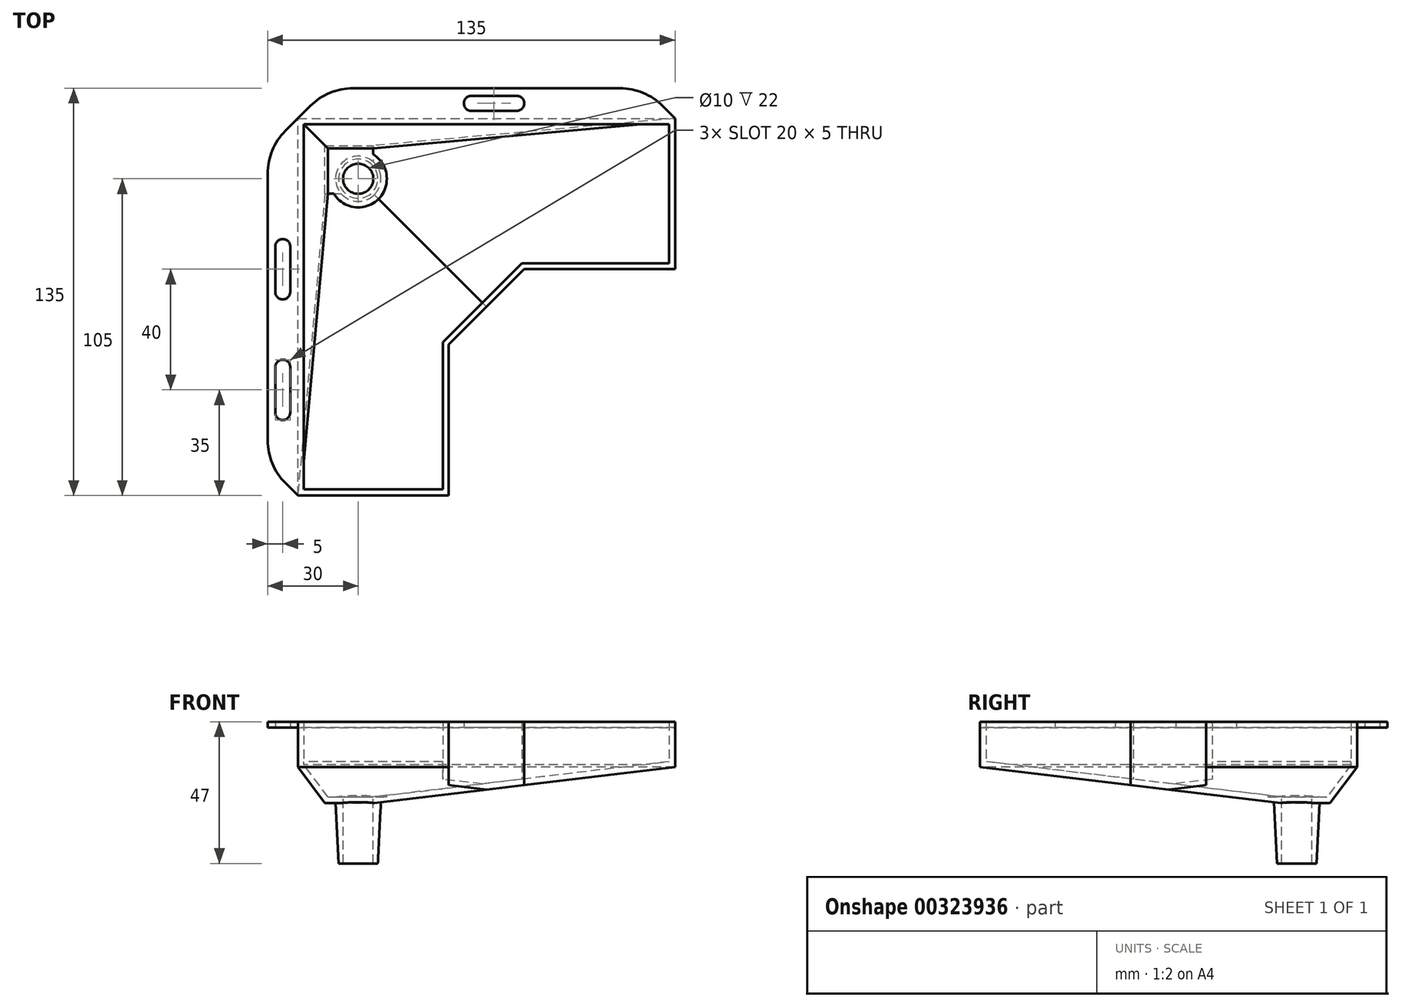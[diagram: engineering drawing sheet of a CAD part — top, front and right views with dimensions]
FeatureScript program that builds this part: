
annotation { "Feature Type Name" : "Feature", "Feature Type Description" : "" }
export const myFeature = defineFeature(function(context is Context, id is Id, definition is map)
    precondition{}
    {
        {
            var Q0;
            Q0=qCreatedBy(makeId("Top.planeOp"),FACE);
            var sketch = newSketch(context, id + "F0", { "sketchPlane" : qUnion([Q0])});
            skLineSegment(sketch, "E0", {"start": v(-70, -85) * mm, "end": v(-70, 40) * mm});
            skLineSegment(sketch, "E1", {"start": v(-70, 40) * mm, "end": v(55, 40) * mm});
            skLineSegment(sketch, "E2", {"start": v(55, 40) * mm, "end": v(55, -10) * mm});
            skLineSegment(sketch, "E3", {"start": v(55, -10) * mm, "end": v(5, -10) * mm});
            skLineSegment(sketch, "E4", {"start": v(5, -10) * mm, "end": v(-20, -35) * mm});
            skLineSegment(sketch, "E5", {"start": v(-20, -35) * mm, "end": v(-20, -85) * mm});
            skLineSegment(sketch, "E6", {"start": v(-20, -85) * mm, "end": v(-70, -85) * mm});
            skLineSegment(sketch, "E7", {"start": v(55, 40) * mm, "end": v(55, 50) * mm});
            skLineSegment(sketch, "E8", {"start": v(55, 50) * mm, "end": v(-80, 50) * mm});
            skLineSegment(sketch, "E9", {"start": v(-80, 50) * mm, "end": v(-80, -85) * mm});
            skLineSegment(sketch, "E10", {"start": v(-80, -85) * mm, "end": v(-70, -85) * mm});
            skCircle(sketch, "E11", {"center": v(-50, 20) * mm, "radius": 7.5 * mm});
            skCircle(sketch, "E12", {"center": v(-50, 20) * mm, "radius": 6 * mm});
            skCircle(sketch, "E13", {"center": v(-50, 20) * mm, "radius": 5 * mm});
            skSolve(sketch);
        }
        {
            var Q0;
            Q0=makeQuery(id+"F0.imprint","IMPRINT",FACE,{"disambiguationData":[TD([[makeQuery(id+"F0.imprint","IMPRINT",EDGE,{"derivedFrom":sQuery(id+"F0.wireOp",EDGE,"E0")}),1.0]])]});
            extrude(context, id + "F1", {"entities" : qUnion([Q0]), "depth" : 2 * mm});
        }
        {
            var Q0;
            Q0=makeQuery(id+"F0.imprint","IMPRINT",FACE,{"disambiguationData":[TD([[makeQuery(id+"F0.imprint","IMPRINT",EDGE,{"derivedFrom":sQuery(id+"F0.wireOp",EDGE,"E0")}),-1.0]])]});
            extrude(context, id + "F2", {"entities" : qUnion([Q0]), "operationType" : NewBodyOperationType.ADD, "depth" : 2 * mm, "hasSecondDirection" : true, "secondDirectionOppositeDirection" : true, "secondDirectionDepth" : 25 * mm});
        }
        {
            var Q0;
            Q0=makeQuery(id+"F0.imprint","IMPRINT",FACE,{"disambiguationData":[TD([[makeQuery(id+"F0.imprint","IMPRINT",EDGE,{"derivedFrom":sQuery(id+"F0.wireOp",EDGE,"E11")}),1.0]])]});
            var Q1;
            Q1=makeQuery(id+"F0.imprint","IMPRINT",FACE,{"disambiguationData":[TD([[makeQuery(id+"F0.imprint","IMPRINT",EDGE,{"derivedFrom":sQuery(id+"F0.wireOp",EDGE,"E12")}),1.0]])]});
            extrude(context, id + "F3", {"entities" : qUnion([Q0, Q1]), "operationType" : NewBodyOperationType.ADD, "oppositeDirection" : true, "depth" : 45 * mm, "hasSecondDirection" : true, "secondDirectionOppositeDirection" : true, "secondDirectionDepth" : 23 * mm});
        }
        {
            var Q0;
            Q0=makeQuery(id+"F3.opExtrude","CAP_EDGE",EDGE,{"disambiguationData":[OSD([sQuery(id+"F0.wireOp",EDGE,"E11")])],"isStart":false});
            chamfer(context, id + "F4", {"entities" : qUnion([Q0]), "chamferType" : ChamferType.TWO_OFFSETS, "width1" : 20 * mm, "oppositeDirection" : false, "width2" : 1 * mm, "tangentPropagation" : true});
        }
        {
            var Q0;
            Q0=makeQuery(id+"F2.opExtrude","CAP_EDGE",EDGE,{"disambiguationData":[OSD([sQuery(id+"F0.wireOp",EDGE,"E2")])],"isStart":true});
            var Q1;
            Q1=makeQuery(id+"F2.opExtrude","CAP_EDGE",EDGE,{"disambiguationData":[OSD([sQuery(id+"F0.wireOp",EDGE,"E6")])],"isStart":true});
            chamfer(context, id + "F5", {"entities" : qUnion([Q0, Q1]), "chamferType" : ChamferType.TWO_OFFSETS, "width1" : 100 * mm, "oppositeDirection" : false, "width2" : 12 * mm, "tangentPropagation" : true});
        }
        {
            var Q0;
            Q0=makeQuery(id+"F2.opExtrude","CAP_EDGE",EDGE,{"disambiguationData":[OSD([sQuery(id+"F0.wireOp",EDGE,"E0")])],"isStart":true});
            var Q1;
            Q1=makeQuery(id+"F2.opExtrude","CAP_EDGE",EDGE,{"disambiguationData":[OSD([sQuery(id+"F0.wireOp",EDGE,"E1")])],"isStart":true});
            chamfer(context, id + "F6", {"entities" : qUnion([Q0, Q1]), "chamferType" : ChamferType.TWO_OFFSETS, "width1" : 9 * mm, "oppositeDirection" : false, "width2" : 12 * mm, "tangentPropagation" : true});
        }
        {
            var Q0;
            {var subQ0=sQuery(id+"F0.wireOp",EDGE,"E1");var subQ1=sQuery(id+"F0.wireOp",EDGE,"E0");Q0=makeQuery(id+"F2.boolean.opBoolean","MERGE",FACE,{"derivedFrom":[makeQuery(id+"F1.opExtrude","CAP_FACE",FACE,{"disambiguationData":[OSD([subQ1,subQ0,sQuery(id+"F0.wireOp",EDGE,"E7"),sQuery(id+"F0.wireOp",EDGE,"E8"),sQuery(id+"F0.wireOp",EDGE,"E9"),sQuery(id+"F0.wireOp",EDGE,"E10")])],"isStart":false}),makeQuery(id+"F2.opExtrude","CAP_FACE",FACE,{"disambiguationData":[OSD([subQ1,subQ0,sQuery(id+"F0.wireOp",EDGE,"E2"),sQuery(id+"F0.wireOp",EDGE,"E3"),sQuery(id+"F0.wireOp",EDGE,"E4"),sQuery(id+"F0.wireOp",EDGE,"E5"),sQuery(id+"F0.wireOp",EDGE,"E6"),sQuery(id+"F0.wireOp",EDGE,"E11")])],"isStart":false})]});}
            shell(context, id + "F7", {"entities" : qUnion([Q0]), "thickness" : 2 * mm});
        }
        {
            var Q0;
            {var subQ0=sQuery(id+"F0.wireOp",EDGE,"E1");var subQ1=sQuery(id+"F0.wireOp",EDGE,"E0");Q0=makeQuery(id+"F2.boolean.opBoolean","MERGE",FACE,{"derivedFrom":[makeQuery(id+"F1.opExtrude","CAP_FACE",FACE,{"disambiguationData":[OSD([subQ1,subQ0,sQuery(id+"F0.wireOp",EDGE,"E7"),sQuery(id+"F0.wireOp",EDGE,"E8"),sQuery(id+"F0.wireOp",EDGE,"E9"),sQuery(id+"F0.wireOp",EDGE,"E10")])],"isStart":false}),makeQuery(id+"F2.opExtrude","CAP_FACE",FACE,{"disambiguationData":[OSD([subQ1,subQ0,sQuery(id+"F0.wireOp",EDGE,"E2"),sQuery(id+"F0.wireOp",EDGE,"E3"),sQuery(id+"F0.wireOp",EDGE,"E4"),sQuery(id+"F0.wireOp",EDGE,"E5"),sQuery(id+"F0.wireOp",EDGE,"E6"),sQuery(id+"F0.wireOp",EDGE,"E11")])],"isStart":false})]});}
            extrude(context, id + "F8", {"entities" : qUnion([Q0]), "operationType" : NewBodyOperationType.REMOVE, "oppositeDirection" : true, "depth" : 25 * mm});
        }
        {
            var Q0;
            Q0=qCreatedBy(makeId("Top.planeOp"),FACE);
            var sketch = newSketch(context, id + "F9", { "sketchPlane" : qUnion([Q0])});
            skLineSegment(sketch, "E14.bottom", {"start": v(5, 42.5) * mm, "end": v(-15, 42.5) * mm});
            skLineSegment(sketch, "E14.top", {"start": v(5, 47.5) * mm, "end": v(-15, 47.5) * mm});
            skLineSegment(sketch, "E14.left", {"start": v(5, 42.5) * mm, "end": v(5, 47.5) * mm});
            skLineSegment(sketch, "E14.right", {"start": v(-15, 42.5) * mm, "end": v(-15, 47.5) * mm});
            skPoint(sketch, "E14.middle", {"position": v(-5, 45) * mm});
            skLineSegment(sketch, "E15.bottom", {"start": v(-72.5, -20) * mm, "end": v(-77.5, -20) * mm});
            skLineSegment(sketch, "E15.top", {"start": v(-72.5, 0) * mm, "end": v(-77.5, 0) * mm});
            skLineSegment(sketch, "E15.left", {"start": v(-72.5, -20) * mm, "end": v(-72.5, 0) * mm});
            skLineSegment(sketch, "E15.right", {"start": v(-77.5, -20) * mm, "end": v(-77.5, 0) * mm});
            skPoint(sketch, "E15.middle", {"position": v(-75, -10) * mm});
            skLineSegment(sketch, "E16.bottom", {"start": v(-72.5, -60) * mm, "end": v(-77.5, -60) * mm});
            skLineSegment(sketch, "E16.top", {"start": v(-72.5, -40) * mm, "end": v(-77.5, -40) * mm});
            skLineSegment(sketch, "E16.left", {"start": v(-72.5, -60) * mm, "end": v(-72.5, -40) * mm});
            skLineSegment(sketch, "E16.right", {"start": v(-77.5, -60) * mm, "end": v(-77.5, -40) * mm});
            skPoint(sketch, "E16.middle", {"position": v(-75, -50) * mm});
            skSolve(sketch);
        }
        {
            var Q0;
            Q0 = qSketchRegion(id + "F9", true);
            extrude(context, id + "F10", {"entities" : qUnion([Q0]), "operationType" : NewBodyOperationType.REMOVE, "depth" : 25 * mm});
        }
        {
            var Q0;
            Q0=makeQuery(id+"F1.opExtrude","SWEPT_EDGE",EDGE,{"disambiguationData":[OSD([sQuery(id+"F0.wireOp",EDGE,"E8"),sQuery(id+"F0.wireOp",EDGE,"E9")])]});
            chamfer(context, id + "F11", {"entities" : qUnion([Q0]), "width" : 20 * mm, "tangentPropagation" : true});
        }
        {
            var Q0;
            Q0=makeQuery(id+"F1.opExtrude","SWEPT_EDGE",EDGE,{"disambiguationData":[OSD([sQuery(id+"F0.wireOp",EDGE,"E7"),sQuery(id+"F0.wireOp",EDGE,"E8")])]});
            var Q1;
            Q1=makeQuery(id+"F1.opExtrude","SWEPT_EDGE",EDGE,{"disambiguationData":[OSD([sQuery(id+"F0.wireOp",EDGE,"E9"),sQuery(id+"F0.wireOp",EDGE,"E10")])]});
            chamfer(context, id + "F12", {"entities" : qUnion([Q0, Q1]), "width" : 10 * mm, "tangentPropagation" : true});
        }
        {
            var Q0;
            {var subQ0=sQuery(id+"F0.wireOp",EDGE,"E8");Q0=makeQuery(id+"F12.opChamfer","BLEND_EDGE",EDGE,{"blendedFrom":[makeQuery(id+"F1.opExtrude","SWEPT_EDGE",EDGE,{"disambiguationData":[OSD([sQuery(id+"F0.wireOp",EDGE,"E7"),subQ0])]}),makeQuery(id+"F1.opExtrude","SWEPT_FACE",FACE,{"disambiguationData":[OSD([subQ0])]})],"blendedInto":[makeQuery(id+"F1.opExtrude","SWEPT_FACE",FACE,{"disambiguationData":[OSD([subQ0])]})]});}
            var Q1;
            {var subQ0=sQuery(id+"F0.wireOp",EDGE,"E8");Q1=makeQuery(id+"F11.opChamfer","BLEND_EDGE",EDGE,{"blendedFrom":[makeQuery(id+"F1.opExtrude","SWEPT_EDGE",EDGE,{"disambiguationData":[OSD([subQ0,sQuery(id+"F0.wireOp",EDGE,"E9")])]}),makeQuery(id+"F1.opExtrude","SWEPT_FACE",FACE,{"disambiguationData":[OSD([subQ0])]})],"blendedInto":[makeQuery(id+"F1.opExtrude","SWEPT_FACE",FACE,{"disambiguationData":[OSD([subQ0])]})]});}
            var Q2;
            {var subQ0=sQuery(id+"F0.wireOp",EDGE,"E9");Q2=makeQuery(id+"F11.opChamfer","BLEND_EDGE",EDGE,{"blendedFrom":[makeQuery(id+"F1.opExtrude","SWEPT_EDGE",EDGE,{"disambiguationData":[OSD([sQuery(id+"F0.wireOp",EDGE,"E8"),subQ0])]}),makeQuery(id+"F1.opExtrude","SWEPT_FACE",FACE,{"disambiguationData":[OSD([subQ0])]})],"blendedInto":[makeQuery(id+"F1.opExtrude","SWEPT_FACE",FACE,{"disambiguationData":[OSD([subQ0])]})]});}
            var Q3;
            {var subQ0=sQuery(id+"F0.wireOp",EDGE,"E9");Q3=makeQuery(id+"F12.opChamfer","BLEND_EDGE",EDGE,{"blendedFrom":[makeQuery(id+"F1.opExtrude","SWEPT_EDGE",EDGE,{"disambiguationData":[OSD([subQ0,sQuery(id+"F0.wireOp",EDGE,"E10")])]}),makeQuery(id+"F1.opExtrude","SWEPT_FACE",FACE,{"disambiguationData":[OSD([subQ0])]})],"blendedInto":[makeQuery(id+"F1.opExtrude","SWEPT_FACE",FACE,{"disambiguationData":[OSD([subQ0])]})]});}
            fillet(context, id + "F13", {"entities" : qUnion([Q0, Q1, Q2, Q3]), "radius" : 20 * mm, "tangentPropagation" : true, "allowEdgeOverflow" : false});
        }
        {
            var Q0;
            Q0=makeQuery(id+"F10.boolean.opBoolean","COPY",EDGE,{"derivedFrom":makeQuery(id+"F10.opExtrude","SWEPT_EDGE",EDGE,{"disambiguationData":[OSD([sQuery(id+"F9.wireOp",EDGE,"E16.bottom"),sQuery(id+"F9.wireOp",EDGE,"E16.right")])]})});
            var Q1;
            Q1=makeQuery(id+"F10.boolean.opBoolean","COPY",EDGE,{"derivedFrom":makeQuery(id+"F10.opExtrude","SWEPT_EDGE",EDGE,{"disambiguationData":[OSD([sQuery(id+"F9.wireOp",EDGE,"E16.bottom"),sQuery(id+"F9.wireOp",EDGE,"E16.left")])]})});
            var Q2;
            Q2=makeQuery(id+"F10.boolean.opBoolean","COPY",EDGE,{"derivedFrom":makeQuery(id+"F10.opExtrude","SWEPT_EDGE",EDGE,{"disambiguationData":[OSD([sQuery(id+"F9.wireOp",EDGE,"E16.top"),sQuery(id+"F9.wireOp",EDGE,"E16.left")])]})});
            var Q3;
            Q3=makeQuery(id+"F10.boolean.opBoolean","COPY",EDGE,{"derivedFrom":makeQuery(id+"F10.opExtrude","SWEPT_EDGE",EDGE,{"disambiguationData":[OSD([sQuery(id+"F9.wireOp",EDGE,"E16.top"),sQuery(id+"F9.wireOp",EDGE,"E16.right")])]})});
            var Q4;
            Q4=makeQuery(id+"F10.boolean.opBoolean","COPY",EDGE,{"derivedFrom":makeQuery(id+"F10.opExtrude","SWEPT_EDGE",EDGE,{"disambiguationData":[OSD([sQuery(id+"F9.wireOp",EDGE,"E15.top"),sQuery(id+"F9.wireOp",EDGE,"E15.right")])]})});
            var Q5;
            Q5=makeQuery(id+"F10.boolean.opBoolean","COPY",EDGE,{"derivedFrom":makeQuery(id+"F10.opExtrude","SWEPT_EDGE",EDGE,{"disambiguationData":[OSD([sQuery(id+"F9.wireOp",EDGE,"E15.top"),sQuery(id+"F9.wireOp",EDGE,"E15.left")])]})});
            var Q6;
            Q6=makeQuery(id+"F10.boolean.opBoolean","COPY",EDGE,{"derivedFrom":makeQuery(id+"F10.opExtrude","SWEPT_EDGE",EDGE,{"disambiguationData":[OSD([sQuery(id+"F9.wireOp",EDGE,"E15.bottom"),sQuery(id+"F9.wireOp",EDGE,"E15.right")])]})});
            var Q7;
            Q7=makeQuery(id+"F10.boolean.opBoolean","COPY",EDGE,{"derivedFrom":makeQuery(id+"F10.opExtrude","SWEPT_EDGE",EDGE,{"disambiguationData":[OSD([sQuery(id+"F9.wireOp",EDGE,"E15.bottom"),sQuery(id+"F9.wireOp",EDGE,"E15.left")])]})});
            var Q8;
            Q8=makeQuery(id+"F10.boolean.opBoolean","COPY",EDGE,{"derivedFrom":makeQuery(id+"F10.opExtrude","SWEPT_EDGE",EDGE,{"disambiguationData":[OSD([sQuery(id+"F9.wireOp",EDGE,"E14.top"),sQuery(id+"F9.wireOp",EDGE,"E14.left")])]})});
            var Q9;
            Q9=makeQuery(id+"F10.boolean.opBoolean","COPY",EDGE,{"derivedFrom":makeQuery(id+"F10.opExtrude","SWEPT_EDGE",EDGE,{"disambiguationData":[OSD([sQuery(id+"F9.wireOp",EDGE,"E14.bottom"),sQuery(id+"F9.wireOp",EDGE,"E14.left")])]})});
            var Q10;
            Q10=makeQuery(id+"F10.boolean.opBoolean","COPY",EDGE,{"derivedFrom":makeQuery(id+"F10.opExtrude","SWEPT_EDGE",EDGE,{"disambiguationData":[OSD([sQuery(id+"F9.wireOp",EDGE,"E14.top"),sQuery(id+"F9.wireOp",EDGE,"E14.right")])]})});
            var Q11;
            Q11=makeQuery(id+"F10.boolean.opBoolean","COPY",EDGE,{"derivedFrom":makeQuery(id+"F10.opExtrude","SWEPT_EDGE",EDGE,{"disambiguationData":[OSD([sQuery(id+"F9.wireOp",EDGE,"E14.bottom"),sQuery(id+"F9.wireOp",EDGE,"E14.right")])]})});
            fillet(context, id + "F14", {"entities" : qUnion([Q0, Q1, Q2, Q3, Q4, Q5, Q6, Q7, Q8, Q9, Q10, Q11]), "radius" : 2.5 * mm, "tangentPropagation" : true, "allowEdgeOverflow" : false});
        }
    });
